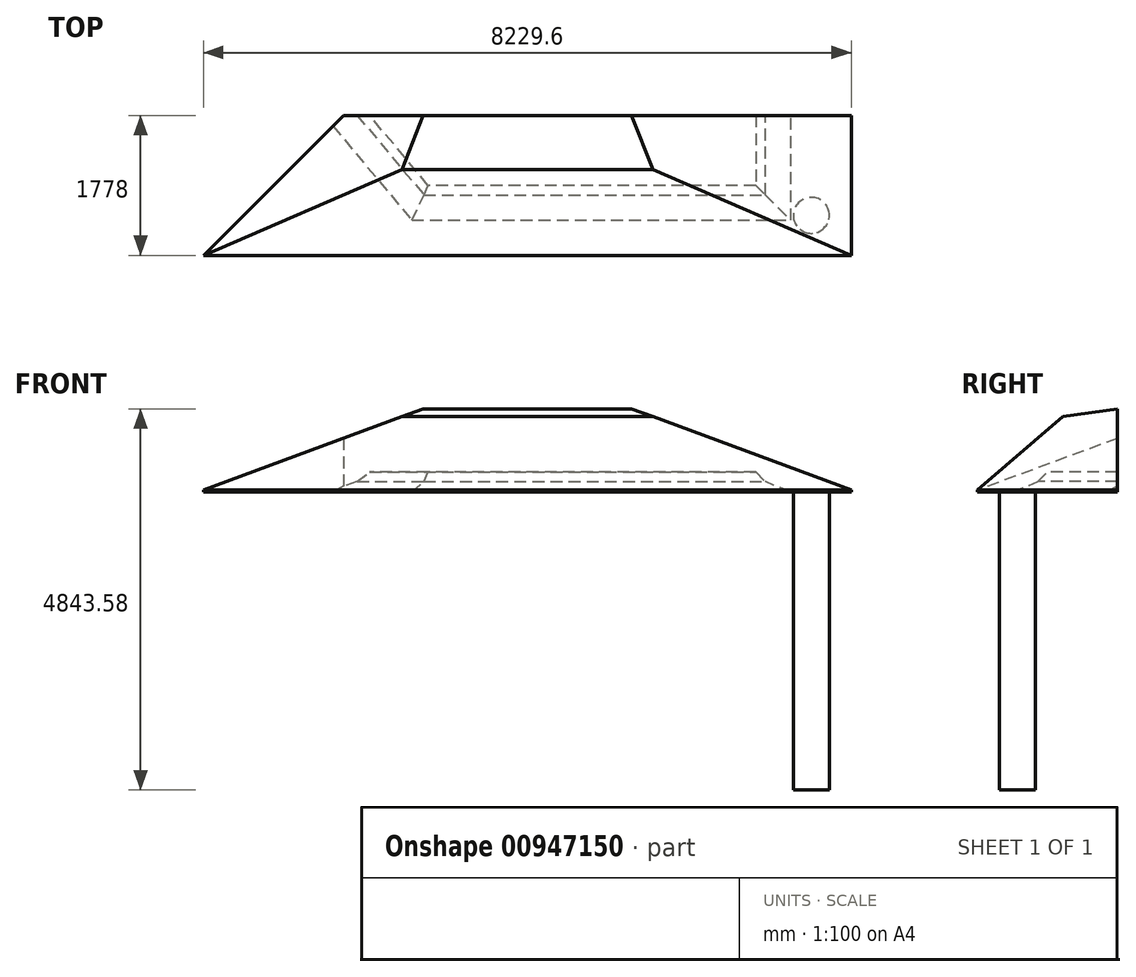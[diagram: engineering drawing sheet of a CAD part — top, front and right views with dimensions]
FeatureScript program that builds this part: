
annotation { "Feature Type Name" : "Feature", "Feature Type Description" : "" }
export const myFeature = defineFeature(function(context is Context, id is Id, definition is map)
    precondition{}
    {
        {
            var Q0;
            Q0=qCreatedBy(makeId("Top.planeOp"),FACE);
            var sketch = newSketch(context, id + "F0", { "sketchPlane" : qUnion([Q0])});
            skLineSegment(sketch, "E0.bottom", {"start": v(0, 0) * mm, "end": v(8229.6, 0) * mm});
            skLineSegment(sketch, "E0.top", {"start": v(0, 1778) * mm, "end": v(8229.6, 1778) * mm});
            skLineSegment(sketch, "E0.left", {"start": v(0, 0) * mm, "end": v(0, 1778) * mm});
            skLineSegment(sketch, "E0.right", {"start": v(8229.6, 0) * mm, "end": v(8229.6, 1778) * mm});
            skLineSegment(sketch, "E1", {"start": v(0, 0) * mm, "end": v(1778, 1778) * mm});
            skSolve(sketch);
        }
        {
            var Q0;
            Q0=makeQuery(id+"F0.imprint","IMPRINT",FACE,{"disambiguationData":[TD([[makeQuery(id+"F0.imprint","IMPRINT",EDGE,{"derivedFrom":sQuery(id+"F0.wireOp",EDGE,"E0.bottom")}),1.0]])]});
            extrude(context, id + "F1", {"entities" : qUnion([Q0]), "depth" : 1524 * mm, "offsetDistance" : 25.4 * mm});
        }
        {
            var Q0;
            Q0=makeQuery(id+"F1.opExtrude","SWEPT_FACE",FACE,{"disambiguationData":[OSD([sQuery(id+"F0.wireOp",EDGE,"E0.bottom")])]});
            var sketch = newSketch(context, id + "F2", { "sketchPlane" : qUnion([Q0])});
            skLineSegment(sketch, "E2", {"start": v(0, 0) * mm, "end": v(4114.8, 1524) * mm});
            skLineSegment(sketch, "E3", {"start": v(4114.8, 1524) * mm, "end": v(8229.6, 0) * mm});
            skLineSegment(sketch, "E4", {"start": v(0, 0) * mm, "end": v(0, 1524) * mm});
            skLineSegment(sketch, "E5", {"start": v(0, 1524) * mm, "end": v(8229.6, 1524) * mm});
            skLineSegment(sketch, "E6", {"start": v(8229.6, 1524) * mm, "end": v(8229.6, 0) * mm});
            skSolve(sketch);
        }
        {
            var Q0;
            Q0 = qSketchRegion(id + "F2", true);
            extrude(context, id + "F3", {"entities" : qUnion([Q0]), "operationType" : NewBodyOperationType.REMOVE, "oppositeDirection" : true, "depth" : 2540 * mm, "offsetDistance" : 25.4 * mm});
        }
        {
            var Q0;
            Q0=qCreatedBy(makeId("Right.planeOp"),FACE);
            var sketch = newSketch(context, id + "F4", { "sketchPlane" : qUnion([Q0])});
            skLineSegment(sketch, "E7", {"start": v(0, 0) * mm, "end": v(1778.36, 1524.18) * mm});
            skLineSegment(sketch, "E8", {"start": v(1778.36, 1524.18) * mm, "end": v(1778.36, 0) * mm});
            skLineSegment(sketch, "E9", {"start": v(0, 0) * mm, "end": v(1778.36, 0) * mm});
            skLineSegment(sketch, "E10", {"start": v(1778.36, 1524.18) * mm, "end": v(0, 1524.18) * mm});
            skLineSegment(sketch, "E11", {"start": v(0, 1524.18) * mm, "end": v(0, 0) * mm});
            skSolve(sketch);
        }
        {
            var Q0;
            Q0=makeQuery(id+"F4.imprint","IMPRINT",FACE,{"disambiguationData":[TD([[makeQuery(id+"F4.imprint","IMPRINT",EDGE,{"derivedFrom":sQuery(id+"F4.wireOp",EDGE,"E7")}),1.0]])]});
            extrude(context, id + "F5", {"entities" : qUnion([Q0]), "operationType" : NewBodyOperationType.REMOVE, "depth" : 8737.6 * mm, "offsetDistance" : 25.4 * mm});
        }
        {
            var Q0;
            Q0=makeQuery(id+"F1.opExtrude","CAP_FACE",FACE,{"disambiguationData":[OSD([sQuery(id+"F0.wireOp",EDGE,"E0.bottom"),sQuery(id+"F0.wireOp",EDGE,"E0.top"),sQuery(id+"F0.wireOp",EDGE,"E0.right"),sQuery(id+"F0.wireOp",EDGE,"E1")])],"isStart":true});
            var sketch = newSketch(context, id + "F6", { "sketchPlane" : qUnion([Q0])});
            skCircle(sketch, "E12", {"center": v(7721.6, -508) * mm, "radius": 228.6 * mm});
            skSolve(sketch);
        }
        {
            var Q0;
            Q0 = qSketchRegion(id + "F6", true);
            extrude(context, id + "F7", {"entities" : qUnion([Q0]), "operationType" : NewBodyOperationType.ADD, "depth" : 3810 * mm, "offsetDistance" : 25.4 * mm});
        }
        {
            var Q0;
            Q0=qCreatedBy(makeId("Right.planeOp"),FACE);
            var sketch = newSketch(context, id + "F8", { "sketchPlane" : qUnion([Q0])});
            skLineSegment(sketch, "E13.bottom", {"start": v(0, 0) * mm, "end": v(1786.98, 0) * mm});
            skLineSegment(sketch, "E13.top", {"start": v(0, 1550.66) * mm, "end": v(1786.98, 1550.66) * mm});
            skLineSegment(sketch, "E13.left", {"start": v(0, 0) * mm, "end": v(0, 1550.66) * mm});
            skLineSegment(sketch, "E13.right", {"start": v(1786.98, 0) * mm, "end": v(1786.98, 1550.66) * mm});
            skLineSegment(sketch, "E14", {"start": v(1786.98, 775.33) * mm, "end": v(0, 775.33) * mm});
            skLineSegment(sketch, "E15", {"start": v(1786.98, 1034.88) * mm, "end": v(0, 775.33) * mm});
            skSolve(sketch);
        }
        {
            var Q0;
            {var subQ0=sQuery(id+"F8.wireOp",EDGE,"E13.top");Q0=makeQuery(id+"F8.imprint","IMPRINT",FACE,{"disambiguationData":[TD([[makeQuery(id+"F8.imprint","IMPRINT",EDGE,{"derivedFrom":subQ0}),-1.0]])]});}
            extrude(context, id + "F9", {"entities" : qUnion([Q0]), "operationType" : NewBodyOperationType.REMOVE, "depth" : 11633.2 * mm, "offsetDistance" : 25.4 * mm});
        }
        {
            var Q0;
            Q0=makeQuery(id+"F1.opExtrude","CAP_FACE",FACE,{"disambiguationData":[OSD([sQuery(id+"F0.wireOp",EDGE,"E0.bottom"),sQuery(id+"F0.wireOp",EDGE,"E0.top"),sQuery(id+"F0.wireOp",EDGE,"E0.right"),sQuery(id+"F0.wireOp",EDGE,"E1")])],"isStart":true});
            extrude(context, id + "F10", {"entities" : qUnion([Q0]), "operationType" : NewBodyOperationType.ADD, "depth" : 25.4 * mm, "offsetDistance" : 25.4 * mm});
        }
        {
            var Q0;
            Q0=makeQuery(id+"F10.opExtrude","CAP_FACE",FACE,{"disambiguationData":[OSD([sQuery(id+"F0.wireOp",EDGE,"E0.bottom"),sQuery(id+"F0.wireOp",EDGE,"E0.top"),sQuery(id+"F0.wireOp",EDGE,"E0.right"),sQuery(id+"F0.wireOp",EDGE,"E1")])],"isStart":false});
            var sketch = newSketch(context, id + "F11", { "sketchPlane" : qUnion([Q0])});
            skLineSegment(sketch, "E16.bottom", {"start": v(1778, -1778) * mm, "end": v(8229.6, -1778) * mm});
            skLineSegment(sketch, "E16.top", {"start": v(1778, -635) * mm, "end": v(8229.6, -635) * mm});
            skLineSegment(sketch, "E16.left", {"start": v(1778, -1778) * mm, "end": v(1778, -635) * mm});
            skLineSegment(sketch, "E16.right", {"start": v(8229.6, -1778) * mm, "end": v(8229.6, -635) * mm});
            skCircle(sketch, "E17", {"center": v(7721.6, -508) * mm, "radius": 232.68 * mm});
            skLineSegment(sketch, "E18", {"start": v(1778, -1778) * mm, "end": v(2737.1, -635) * mm});
            skLineSegment(sketch, "E19", {"start": v(8229.6, -1778) * mm, "end": v(7270.5, -635) * mm});
            skLineSegment(sketch, "E20", {"start": v(7270.5, -635) * mm, "end": v(7270.5, -1778) * mm});
            skSolve(sketch);
        }
        {
            var Q0;
            {var subQ0=sQuery(id+"F11.wireOp",EDGE,"E18");Q0=makeQuery(id+"F11.imprint","IMPRINT",FACE,{"disambiguationData":[TD([[makeQuery(id+"F11.imprint","IMPRINT",EDGE,{"derivedFrom":subQ0}),-1.0]])]});}
            extrude(context, id + "F12", {"entities" : qUnion([Q0]), "operationType" : NewBodyOperationType.REMOVE, "oppositeDirection" : true, "depth" : 254 * mm, "offsetDistance" : 25.4 * mm});
        }
        {
            var Q0;
            Q0=makeQuery(id+"F12.boolean.opBoolean","COPY",EDGE,{"derivedFrom":makeQuery(id+"F12.opExtrude","CAP_EDGE",EDGE,{"disambiguationData":[OSD([sQuery(id+"F11.wireOp",EDGE,"E20")])],"isStart":false})});
            var Q1;
            Q1=makeQuery(id+"F12.boolean.opBoolean","COPY",EDGE,{"derivedFrom":makeQuery(id+"F12.opExtrude","CAP_EDGE",EDGE,{"disambiguationData":[OSD([sQuery(id+"F11.wireOp",EDGE,"E16.top")])],"isStart":false})});
            var Q2;
            Q2=makeQuery(id+"F12.boolean.opBoolean","COPY",EDGE,{"derivedFrom":makeQuery(id+"F12.opExtrude","CAP_EDGE",EDGE,{"disambiguationData":[OSD([sQuery(id+"F11.wireOp",EDGE,"E18")])],"isStart":false})});
            chamfer(context, id + "F13", {"entities" : qUnion([Q0, Q1, Q2]), "width" : 254 * mm, "tangentPropagation" : true});
        }
        {
            var Q0;
            Q0=makeQuery(id+"F13.opChamfer","BLEND_EDGE",EDGE,{"blendedFrom":[makeQuery(id+"F12.boolean.opBoolean","COPY",EDGE,{"derivedFrom":makeQuery(id+"F12.opExtrude","CAP_EDGE",EDGE,{"disambiguationData":[OSD([sQuery(id+"F11.wireOp",EDGE,"E18")])],"isStart":false})}),makeQuery(id+"F10.opExtrude","CAP_FACE",FACE,{"disambiguationData":[OSD([sQuery(id+"F0.wireOp",EDGE,"E0.bottom"),sQuery(id+"F0.wireOp",EDGE,"E0.top"),sQuery(id+"F0.wireOp",EDGE,"E0.right"),sQuery(id+"F0.wireOp",EDGE,"E1")])],"isStart":false})],"blendedInto":[makeQuery(id+"F10.opExtrude","CAP_FACE",FACE,{"disambiguationData":[OSD([sQuery(id+"F0.wireOp",EDGE,"E0.bottom"),sQuery(id+"F0.wireOp",EDGE,"E0.top"),sQuery(id+"F0.wireOp",EDGE,"E0.right"),sQuery(id+"F0.wireOp",EDGE,"E1")])],"isStart":false})]});
            var Q1;
            Q1=makeQuery(id+"F13.opChamfer","BLEND_EDGE",EDGE,{"blendedFrom":[makeQuery(id+"F12.boolean.opBoolean","COPY",EDGE,{"derivedFrom":makeQuery(id+"F12.opExtrude","CAP_EDGE",EDGE,{"disambiguationData":[OSD([sQuery(id+"F11.wireOp",EDGE,"E16.top")])],"isStart":false})}),makeQuery(id+"F10.opExtrude","CAP_FACE",FACE,{"disambiguationData":[OSD([sQuery(id+"F0.wireOp",EDGE,"E0.bottom"),sQuery(id+"F0.wireOp",EDGE,"E0.top"),sQuery(id+"F0.wireOp",EDGE,"E0.right"),sQuery(id+"F0.wireOp",EDGE,"E1")])],"isStart":false})],"blendedInto":[makeQuery(id+"F10.opExtrude","CAP_FACE",FACE,{"disambiguationData":[OSD([sQuery(id+"F0.wireOp",EDGE,"E0.bottom"),sQuery(id+"F0.wireOp",EDGE,"E0.top"),sQuery(id+"F0.wireOp",EDGE,"E0.right"),sQuery(id+"F0.wireOp",EDGE,"E1")])],"isStart":false})]});
            var Q2;
            Q2=makeQuery(id+"F13.opChamfer","BLEND_EDGE",EDGE,{"blendedFrom":[makeQuery(id+"F12.boolean.opBoolean","COPY",EDGE,{"derivedFrom":makeQuery(id+"F12.opExtrude","CAP_EDGE",EDGE,{"disambiguationData":[OSD([sQuery(id+"F11.wireOp",EDGE,"E20")])],"isStart":false})}),makeQuery(id+"F10.opExtrude","CAP_FACE",FACE,{"disambiguationData":[OSD([sQuery(id+"F0.wireOp",EDGE,"E0.bottom"),sQuery(id+"F0.wireOp",EDGE,"E0.top"),sQuery(id+"F0.wireOp",EDGE,"E0.right"),sQuery(id+"F0.wireOp",EDGE,"E1")])],"isStart":false})],"blendedInto":[makeQuery(id+"F10.opExtrude","CAP_FACE",FACE,{"disambiguationData":[OSD([sQuery(id+"F0.wireOp",EDGE,"E0.bottom"),sQuery(id+"F0.wireOp",EDGE,"E0.top"),sQuery(id+"F0.wireOp",EDGE,"E0.right"),sQuery(id+"F0.wireOp",EDGE,"E1")])],"isStart":false})]});
            chamfer(context, id + "F14", {"entities" : qUnion([Q0, Q1, Q2]), "width" : 457.2 * mm, "tangentPropagation" : true});
        }
    });
